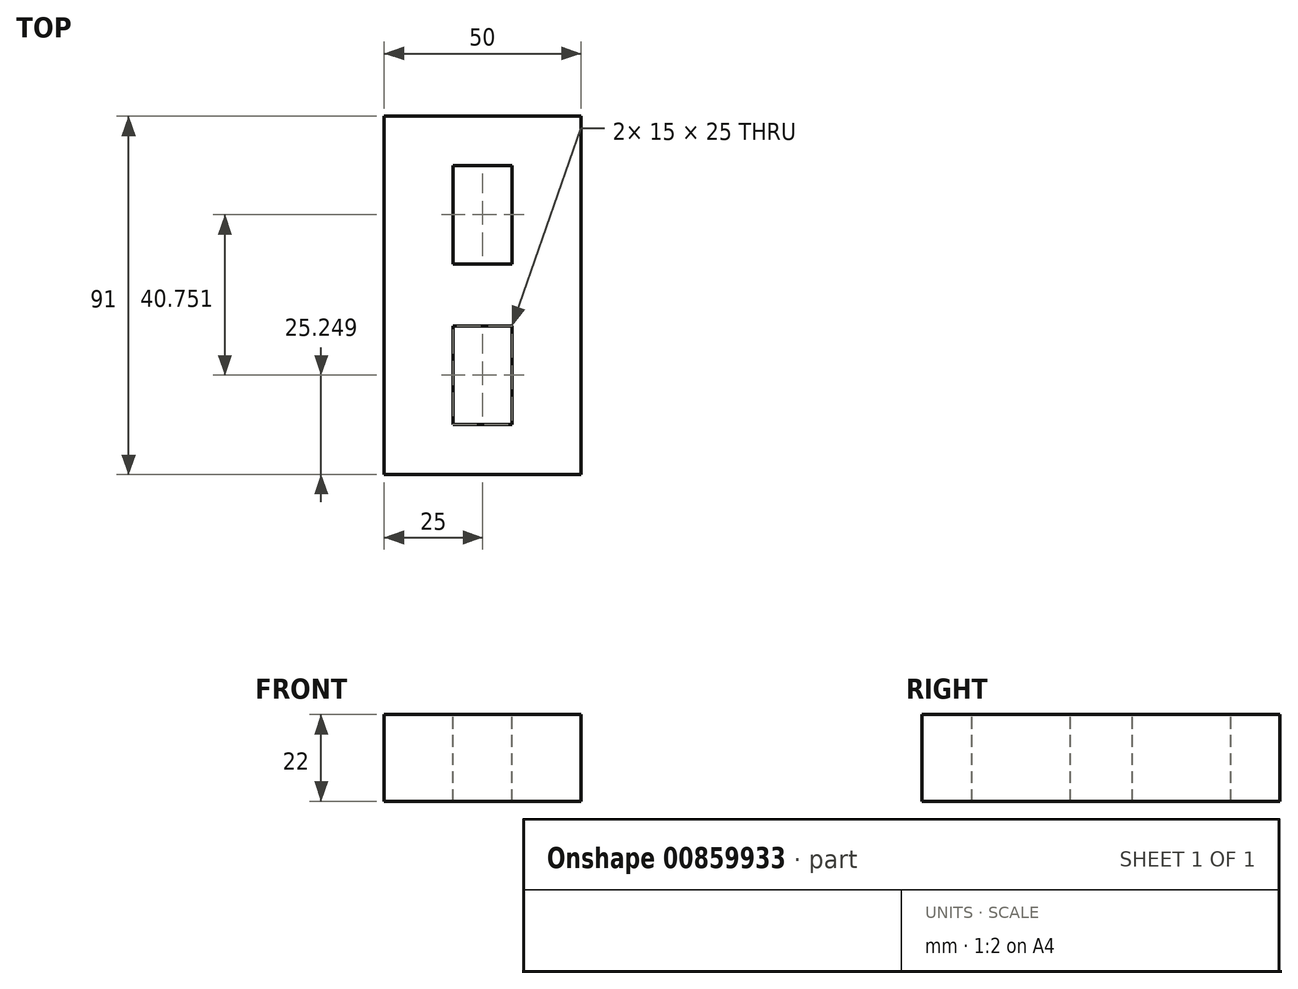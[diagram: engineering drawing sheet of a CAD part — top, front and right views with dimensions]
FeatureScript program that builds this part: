
annotation { "Feature Type Name" : "Feature", "Feature Type Description" : "" }
export const myFeature = defineFeature(function(context is Context, id is Id, definition is map)
    precondition{}
    {
        {
            var Q0;
            Q0=qCreatedBy(makeId("Top.planeOp"),FACE);
            var sketch = newSketch(context, id + "F0", { "sketchPlane" : qUnion([Q0])});
            skLineSegment(sketch, "E0.bottom", {"start": v(25, -25) * mm, "end": v(-25, -25) * mm});
            skLineSegment(sketch, "E0.top", {"start": v(25, 25) * mm, "end": v(-25, 25) * mm});
            skLineSegment(sketch, "E0.left", {"start": v(25, -25) * mm, "end": v(25, 25) * mm});
            skLineSegment(sketch, "E0.right", {"start": v(-25, -25) * mm, "end": v(-25, 25) * mm});
            skPoint(sketch, "E0.middle", {"position": v(0, 0) * mm});
            skSolve(sketch);
        }
        {
            var Q0;
            Q0=makeQuery(id+"F0.imprint","IMPRINT",FACE,{"disambiguationData":[TD([[makeQuery(id+"F0.imprint","IMPRINT",EDGE,{"derivedFrom":sQuery(id+"F0.wireOp",EDGE,"E0.bottom")}),-1.0]])]});
            extrude(context, id + "F1", {"entities" : qUnion([Q0]), "depth" : 5 * mm, "offsetDistance" : 25 * mm});
        }
        {
            var Q0;
            Q0=makeQuery(id+"F1.opExtrude","CAP_FACE",FACE,{"disambiguationData":[OSD([sQuery(id+"F0.wireOp",EDGE,"E0.bottom"),sQuery(id+"F0.wireOp",EDGE,"E0.top"),sQuery(id+"F0.wireOp",EDGE,"E0.left"),sQuery(id+"F0.wireOp",EDGE,"E0.right")])],"isStart":false});
            var sketch = newSketch(context, id + "F2", { "sketchPlane" : qUnion([Q0])});
            skLineSegment(sketch, "E1.bottom", {"start": v(7.5, -12.5) * mm, "end": v(-7.5, -12.5) * mm});
            skLineSegment(sketch, "E1.top", {"start": v(7.5, 12.5) * mm, "end": v(-7.5, 12.5) * mm});
            skLineSegment(sketch, "E1.left", {"start": v(7.5, -12.5) * mm, "end": v(7.5, 12.5) * mm});
            skLineSegment(sketch, "E1.right", {"start": v(-7.5, -12.5) * mm, "end": v(-7.5, 12.5) * mm});
            skPoint(sketch, "E1.middle", {"position": v(0, 0) * mm});
            skSolve(sketch);
        }
        {
            var Q0;
            Q0=makeQuery(id+"F2.imprint","IMPRINT",FACE,{"disambiguationData":[TD([[makeQuery(id+"F2.imprint","IMPRINT",EDGE,{"derivedFrom":sQuery(id+"F2.wireOp",EDGE,"E1.bottom")}),-1.0]])]});
            extrude(context, id + "F3", {"entities" : qUnion([Q0]), "operationType" : NewBodyOperationType.REMOVE, "oppositeDirection" : true, "depth" : 169 * mm, "offsetDistance" : 25 * mm});
        }
        {
            var Q0;
            Q0=makeQuery(id+"F1.opExtrude","CAP_FACE",FACE,{"disambiguationData":[OSD([sQuery(id+"F0.wireOp",EDGE,"E0.bottom"),sQuery(id+"F0.wireOp",EDGE,"E0.top"),sQuery(id+"F0.wireOp",EDGE,"E0.left"),sQuery(id+"F0.wireOp",EDGE,"E0.right")])],"isStart":false});
            extrude(context, id + "F4", {"entities" : qUnion([Q0]), "operationType" : NewBodyOperationType.ADD, "depth" : 17 * mm, "offsetDistance" : 25 * mm});
        }
        {
            var Q0;
            {var subQ0=sQuery(id+"F0.wireOp",EDGE,"E0.bottom");Q0=makeQuery(id+"F4.boolean.opBoolean","MERGE",FACE,{"derivedFrom":[makeQuery(id+"F1.opExtrude","SWEPT_FACE",FACE,{"disambiguationData":[OSD([subQ0])]}),makeQuery(id+"F4.opExtrude","SWEPT_FACE",FACE,{"disambiguationData":[OSD([subQ0])]})]});}
            extrude(context, id + "F5", {"entities" : qUnion([Q0]), "operationType" : NewBodyOperationType.ADD, "depth" : 41 * mm, "offsetDistance" : 25 * mm});
        }
        {
            var Q0;
            {var subQ0=sQuery(id+"F0.wireOp",EDGE,"E0.bottom");Q0=makeQuery(id+"F5.boolean.opBoolean","MERGE",FACE,{"derivedFrom":[makeQuery(id+"F4.opExtrude","CAP_FACE",FACE,{"disambiguationData":[OSD([subQ0,sQuery(id+"F0.wireOp",EDGE,"E0.top"),sQuery(id+"F0.wireOp",EDGE,"E0.left"),sQuery(id+"F0.wireOp",EDGE,"E0.right")])],"isStart":false}),makeQuery(id+"F5.opExtrude","SWEPT_FACE",FACE,{"disambiguationData":[OSD([subQ0]),TDD([makeQuery(id+"F4.opExtrude","CAP_EDGE",EDGE,{"disambiguationData":[OSD([subQ0])],"isStart":false})])]})]});}
            var sketch = newSketch(context, id + "F6", { "sketchPlane" : qUnion([Q0])});
            skLineSegment(sketch, "E2.bottom", {"start": v(7.5, -28.25) * mm, "end": v(-7.5, -28.25) * mm});
            skLineSegment(sketch, "E2.top", {"start": v(7.5, -53.25) * mm, "end": v(-7.5, -53.25) * mm});
            skLineSegment(sketch, "E2.left", {"start": v(7.5, -28.25) * mm, "end": v(7.5, -53.25) * mm});
            skLineSegment(sketch, "E2.right", {"start": v(-7.5, -28.25) * mm, "end": v(-7.5, -53.25) * mm});
            skPoint(sketch, "E2.middle", {"position": v(0, -40.75) * mm});
            skSolve(sketch);
        }
        {
            var Q0;
            Q0=makeQuery(id+"F6.imprint","IMPRINT",FACE,{"disambiguationData":[TD([[makeQuery(id+"F6.imprint","IMPRINT",EDGE,{"derivedFrom":sQuery(id+"F6.wireOp",EDGE,"E2.bottom")}),1.0]])]});
            extrude(context, id + "F7", {"entities" : qUnion([Q0]), "operationType" : NewBodyOperationType.REMOVE, "oppositeDirection" : true, "depth" : 141 * mm, "offsetDistance" : 25 * mm});
        }
    });
